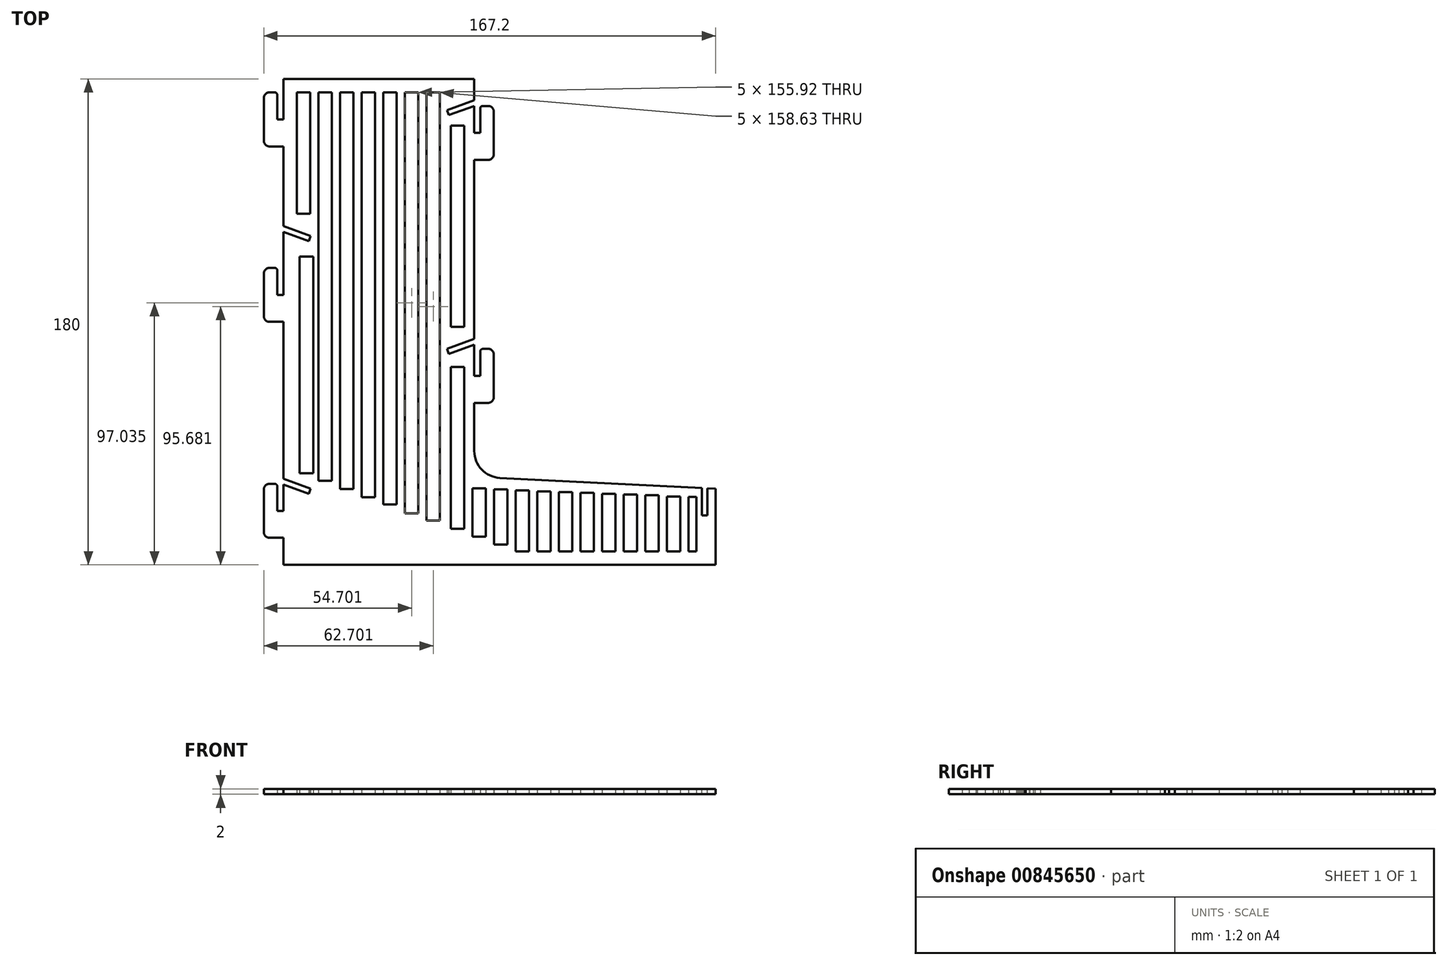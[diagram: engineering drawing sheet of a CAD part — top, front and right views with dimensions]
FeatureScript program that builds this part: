
annotation { "Feature Type Name" : "Feature", "Feature Type Description" : "" }
export const myFeature = defineFeature(function(context is Context, id is Id, definition is map)
    precondition{}
    {
        {
            var Q0;
            Q0=qCreatedBy(makeId("Top.planeOp"),FACE);
            var sketch = newSketch(context, id + "F0", { "sketchPlane" : qUnion([Q0])});
            skLineSegment(sketch, "E0", {"start": v(-80.97, 314.3) * mm, "end": v(-80.97, -331.9) * mm, "construction": true});
            skLineSegment(sketch, "E1", {"start": v(79.03, 327.55) * mm, "end": v(79.03, -337.2) * mm, "construction": true});
            skLineSegment(sketch, "E2", {"start": v(-106.48, 88.93) * mm, "end": v(117.78, 88.93) * mm, "construction": true});
            skLineSegment(sketch, "E3", {"start": v(-139.87, -91.07) * mm, "end": v(208.72, -91.07) * mm, "construction": true});
            skLineSegment(sketch, "E4", {"start": v(-10.29, 120.3) * mm, "end": v(-10.29, -131.57) * mm, "construction": true});
            skLineSegment(sketch, "E5", {"start": v(-224.74, -47.65) * mm, "end": v(82.4, -63.07) * mm, "construction": true});
            skLineSegment(sketch, "E6", {"start": v(-80.97, 88.93) * mm, "end": v(-10.29, 88.93) * mm});
            skLineSegment(sketch, "E7", {"start": v(-10.29, 88.93) * mm, "end": v(-10.29, -58.42) * mm});
            skLineSegment(sketch, "E8", {"start": v(-10.29, -58.42) * mm, "end": v(79.03, -62.9) * mm});
            skLineSegment(sketch, "E9", {"start": v(79.03, -62.9) * mm, "end": v(79.03, -91.07) * mm});
            skLineSegment(sketch, "E10", {"start": v(79.03, -91.07) * mm, "end": v(-80.97, -91.07) * mm});
            skLineSegment(sketch, "E11", {"start": v(-80.97, 88.93) * mm, "end": v(-80.97, -91.07) * mm});
            skSolve(sketch);
        }
        {
            var Q0;
            Q0=qCreatedBy(makeId("Top.planeOp"),FACE);
            var sketch = newSketch(context, id + "F1", { "sketchPlane" : qUnion([Q0])});
            skLineSegment(sketch, "E12.0", {"start": v(-80.97, 88.93) * mm, "end": v(-10.29, 88.93) * mm});
            skLineSegment(sketch, "E12.1", {"start": v(-80.97, 88.93) * mm, "end": v(-80.97, -91.07) * mm});
            skLineSegment(sketch, "E12.2", {"start": v(-10.29, 88.93) * mm, "end": v(-10.29, -48.9) * mm});
            skLineSegment(sketch, "E12.3", {"start": v(-0.79, -58.9) * mm, "end": v(79.03, -62.9) * mm});
            skLineSegment(sketch, "E12.4", {"start": v(79.03, -62.9) * mm, "end": v(79.03, -91.07) * mm});
            skLineSegment(sketch, "E12.5", {"start": v(79.03, -91.07) * mm, "end": v(-80.97, -91.07) * mm});
            skPoint(sketch, "E13.visualSharp", {"position": v(-10.29, -58.42) * mm});
            skArc(sketch, "E13.filletArc", {"start": v(-10.29, -48.9) * mm, "mid": v(-7.53, -55.8) * mm, "end": v(-0.79, -58.9) * mm});
            skSolve(sketch);
        }
        {
            var Q0;
            Q0 = qSketchRegion(id + "F1", true);
            extrude(context, id + "F2", {"entities" : qUnion([Q0]), "depth" : 2 * mm, "offsetDistance" : 25 * mm});
        }
        {
            var Q0;
            Q0=qCreatedBy(makeId("Top.planeOp"),FACE);
            var sketch = newSketch(context, id + "F3", { "sketchPlane" : qUnion([Q0])});
            skLineSegment(sketch, "E14.bottom", {"start": v(-20.37, -11.03) * mm, "end": v(-10.97, -7.61) * mm});
            skLineSegment(sketch, "E14.top", {"start": v(-19.68, -12.91) * mm, "end": v(-10.29, -9.5) * mm});
            skLineSegment(sketch, "E14.left", {"start": v(-20.37, -11.03) * mm, "end": v(-19.68, -12.91) * mm});
            skLineSegment(sketch, "E14.right", {"start": v(-10.97, -7.61) * mm, "end": v(-10.29, -9.5) * mm});
            skLineSegment(sketch, "E15.bottom", {"start": v(-10.97, -7.61) * mm, "end": v(-5.1, -5.47) * mm});
            skLineSegment(sketch, "E15.top", {"start": v(-10.29, -9.5) * mm, "end": v(-4.4, -7.35) * mm});
            skLineSegment(sketch, "E15.right", {"start": v(-5.1, -5.47) * mm, "end": v(-4.4, -7.35) * mm});
            skLineSegment(sketch, "E16.0", {"start": v(-10.29, -9.5) * mm, "end": v(-4.4, -7.35) * mm, "construction": true});
            skLineSegment(sketch, "E17.bottom", {"start": v(-20.37, 77.39) * mm, "end": v(-10.97, 80.8) * mm});
            skLineSegment(sketch, "E17.top", {"start": v(-19.68, 75.5) * mm, "end": v(-10.29, 78.93) * mm});
            skLineSegment(sketch, "E17.left", {"start": v(-20.37, 77.39) * mm, "end": v(-19.68, 75.5) * mm});
            skLineSegment(sketch, "E17.right", {"start": v(-10.97, 80.8) * mm, "end": v(-10.29, 78.93) * mm});
            skLineSegment(sketch, "E18.bottom", {"start": v(-10.97, 80.8) * mm, "end": v(-4, 83.34) * mm});
            skLineSegment(sketch, "E18.top", {"start": v(-10.29, 78.93) * mm, "end": v(-3.31, 81.46) * mm});
            skLineSegment(sketch, "E18.right", {"start": v(-4, 83.34) * mm, "end": v(-3.31, 81.46) * mm});
            skLineSegment(sketch, "E19.0", {"start": v(-10.29, 78.93) * mm, "end": v(-3.31, 81.46) * mm, "construction": true});
            skLineSegment(sketch, "E20.bottom", {"start": v(-71.57, 28.81) * mm, "end": v(-80.97, 32.23) * mm});
            skLineSegment(sketch, "E20.top", {"start": v(-70.89, 30.69) * mm, "end": v(-80.29, 34.1) * mm});
            skLineSegment(sketch, "E20.left", {"start": v(-71.57, 28.81) * mm, "end": v(-70.89, 30.69) * mm});
            skLineSegment(sketch, "E20.right", {"start": v(-80.97, 32.23) * mm, "end": v(-80.29, 34.1) * mm});
            skLineSegment(sketch, "E21.bottom", {"start": v(-80.97, 32.23) * mm, "end": v(-87.94, 34.77) * mm});
            skLineSegment(sketch, "E21.top", {"start": v(-80.29, 34.1) * mm, "end": v(-87.26, 36.65) * mm});
            skLineSegment(sketch, "E21.right", {"start": v(-87.94, 34.77) * mm, "end": v(-87.26, 36.65) * mm});
            skLineSegment(sketch, "E22.0", {"start": v(-87.26, 36.65) * mm, "end": v(-80.29, 34.1) * mm, "construction": true});
            skLineSegment(sketch, "E23.bottom", {"start": v(-71.57, -64.78) * mm, "end": v(-80.97, -61.36) * mm});
            skLineSegment(sketch, "E23.top", {"start": v(-70.89, -62.9) * mm, "end": v(-80.29, -59.48) * mm});
            skLineSegment(sketch, "E23.left", {"start": v(-71.57, -64.78) * mm, "end": v(-70.89, -62.9) * mm});
            skLineSegment(sketch, "E23.right", {"start": v(-80.97, -61.36) * mm, "end": v(-80.29, -59.48) * mm});
            skLineSegment(sketch, "E24.bottom", {"start": v(-80.97, -61.36) * mm, "end": v(-87.94, -58.82) * mm});
            skLineSegment(sketch, "E24.top", {"start": v(-80.29, -59.48) * mm, "end": v(-87.26, -56.94) * mm});
            skLineSegment(sketch, "E24.right", {"start": v(-87.94, -58.82) * mm, "end": v(-87.26, -56.94) * mm});
            skLineSegment(sketch, "E25.0", {"start": v(-87.26, -56.94) * mm, "end": v(-80.29, -59.48) * mm, "construction": true});
            skLineSegment(sketch, "E26.left", {"start": v(-70.89, -62.9) * mm, "end": v(-71.64, -64.97) * mm});
            skLineSegment(sketch, "E27.bottom", {"start": v(74.03, -72.75) * mm, "end": v(74.03, -62.75) * mm});
            skLineSegment(sketch, "E27.top", {"start": v(76.03, -72.75) * mm, "end": v(76.03, -62.75) * mm});
            skLineSegment(sketch, "E27.left", {"start": v(74.03, -72.75) * mm, "end": v(76.03, -72.75) * mm});
            skLineSegment(sketch, "E27.right", {"start": v(74.03, -62.75) * mm, "end": v(76.03, -62.75) * mm});
            skLineSegment(sketch, "E28.bottom", {"start": v(74.03, -62.75) * mm, "end": v(74.03, -55.33) * mm});
            skLineSegment(sketch, "E28.top", {"start": v(76.03, -62.75) * mm, "end": v(76.03, -55.33) * mm});
            skLineSegment(sketch, "E28.right", {"start": v(74.03, -55.33) * mm, "end": v(76.03, -55.33) * mm});
            skLineSegment(sketch, "E29.0", {"start": v(76.03, -55.33) * mm, "end": v(76.03, -62.75) * mm, "construction": true});
            skSolve(sketch);
        }
        {
            var Q0;
            {var subQ0=makeQuery(id+"F3.imprint","IMPRINT",EDGE,{"derivedFrom":sQuery(id+"F3.wireOp",EDGE,"E27.right")});var subQ1=makeQuery(id+"F3.imprint","IMPRINT",EDGE,{"derivedFrom":sQuery(id+"F3.wireOp",EDGE,"E23.right")});var subQ2=makeQuery(id+"F3.imprint","IMPRINT",EDGE,{"derivedFrom":sQuery(id+"F3.wireOp",EDGE,"E20.right")});var subQ3=makeQuery(id+"F3.imprint","IMPRINT",EDGE,{"derivedFrom":sQuery(id+"F3.wireOp",EDGE,"E17.right")});var subQ4=makeQuery(id+"F3.imprint","IMPRINT",EDGE,{"derivedFrom":sQuery(id+"F3.wireOp",EDGE,"E14.right")});Q0=qUnion([makeQuery(id+"F3.imprint","IMPRINT",FACE,{"disambiguationData":[TD([[makeQuery(id+"F3.imprint","IMPRINT",EDGE,{"derivedFrom":sQuery(id+"F3.wireOp",EDGE,"E14.bottom")}),-1.0]])]}),makeQuery(id+"F3.imprint","IMPRINT",FACE,{"disambiguationData":[TD([[subQ4,1.0]])]}),makeQuery(id+"F3.imprint","IMPRINT",FACE,{"disambiguationData":[TD([[makeQuery(id+"F3.imprint","IMPRINT",EDGE,{"derivedFrom":sQuery(id+"F3.wireOp",EDGE,"E17.bottom")}),-1.0]])]}),makeQuery(id+"F3.imprint","IMPRINT",FACE,{"disambiguationData":[TD([[subQ3,1.0]])]}),makeQuery(id+"F3.imprint","IMPRINT",FACE,{"disambiguationData":[TD([[makeQuery(id+"F3.imprint","IMPRINT",EDGE,{"derivedFrom":sQuery(id+"F3.wireOp",EDGE,"E20.bottom")}),-1.0]])]}),makeQuery(id+"F3.imprint","IMPRINT",FACE,{"disambiguationData":[TD([[subQ2,1.0]])]}),makeQuery(id+"F3.imprint","IMPRINT",FACE,{"disambiguationData":[TD([[makeQuery(id+"F3.imprint","IMPRINT",EDGE,{"derivedFrom":sQuery(id+"F3.wireOp",EDGE,"E23.bottom")}),-1.0]])]}),makeQuery(id+"F3.imprint","IMPRINT",FACE,{"disambiguationData":[TD([[subQ1,1.0]])]}),makeQuery(id+"F3.imprint","IMPRINT",FACE,{"disambiguationData":[TD([[makeQuery(id+"F3.imprint","IMPRINT",EDGE,{"derivedFrom":sQuery(id+"F3.wireOp",EDGE,"E27.bottom")}),-1.0]])]}),makeQuery(id+"F3.imprint","IMPRINT",FACE,{"disambiguationData":[TD([[subQ0,1.0]])]})]);}
            extrude(context, id + "F4", {"entities" : qUnion([Q0]), "operationType" : NewBodyOperationType.REMOVE, "depth" : 25 * mm, "offsetDistance" : 25 * mm});
        }
        {
            var Q0;
            Q0=qCreatedBy(makeId("Top.planeOp"),FACE);
            var sketch = newSketch(context, id + "F5", { "sketchPlane" : qUnion([Q0])});
            skLineSegment(sketch, "E30", {"start": v(-86.17, -61.07) * mm, "end": v(-84.2, -61.07) * mm});
            skLineSegment(sketch, "E31", {"start": v(-83.17, -62.1) * mm, "end": v(-83.17, -71.07) * mm});
            skPoint(sketch, "E31.endSnap0", {"position": v(-84.58, -71.07) * mm});
            skLineSegment(sketch, "E32", {"start": v(-83.17, -71.07) * mm, "end": v(-80.97, -71.07) * mm});
            skLineSegment(sketch, "E33", {"start": v(-80.97, -71.07) * mm, "end": v(-80.97, -81.07) * mm});
            skLineSegment(sketch, "E34", {"start": v(-80.97, -81.07) * mm, "end": v(-83.17, -81.07) * mm});
            skLineSegment(sketch, "E35", {"start": v(-83.17, -81.07) * mm, "end": v(-86.17, -81.07) * mm});
            skLineSegment(sketch, "E36", {"start": v(-88.17, -79.07) * mm, "end": v(-88.17, -63.07) * mm});
            skPoint(sketch, "E37.visualSharp", {"position": v(-83.17, -61.07) * mm});
            skArc(sketch, "E37.filletArc", {"start": v(-83.17, -62.1) * mm, "mid": v(-83.47, -61.37) * mm, "end": v(-84.2, -61.07) * mm});
            skPoint(sketch, "E38.visualSharp", {"position": v(-88.17, -61.07) * mm});
            skArc(sketch, "E38.filletArc", {"start": v(-86.17, -61.07) * mm, "mid": v(-87.58, -61.66) * mm, "end": v(-88.17, -63.07) * mm});
            skPoint(sketch, "E39.visualSharp", {"position": v(-88.17, -81.07) * mm});
            skArc(sketch, "E39.filletArc", {"start": v(-88.17, -79.07) * mm, "mid": v(-87.58, -80.49) * mm, "end": v(-86.17, -81.07) * mm});
            skLineSegment(sketch, "E40", {"start": v(-86.17, 18.93) * mm, "end": v(-84.2, 18.93) * mm});
            skLineSegment(sketch, "E41", {"start": v(-83.17, 17.9) * mm, "end": v(-83.17, 8.93) * mm});
            skPoint(sketch, "E41.endSnap0", {"position": v(-84.58, 8.93) * mm});
            skLineSegment(sketch, "E42", {"start": v(-83.17, 8.93) * mm, "end": v(-80.97, 8.93) * mm});
            skLineSegment(sketch, "E43", {"start": v(-80.97, 8.93) * mm, "end": v(-80.97, -1.07) * mm});
            skLineSegment(sketch, "E44", {"start": v(-80.97, -1.07) * mm, "end": v(-83.17, -1.07) * mm});
            skLineSegment(sketch, "E45", {"start": v(-83.17, -1.07) * mm, "end": v(-86.17, -1.07) * mm});
            skLineSegment(sketch, "E46", {"start": v(-88.17, 0.93) * mm, "end": v(-88.17, 16.93) * mm});
            skPoint(sketch, "E47.visualSharp", {"position": v(-83.17, 18.93) * mm});
            skArc(sketch, "E47.filletArc", {"start": v(-83.17, 17.9) * mm, "mid": v(-83.47, 18.63) * mm, "end": v(-84.2, 18.93) * mm});
            skPoint(sketch, "E48.visualSharp", {"position": v(-88.17, 18.93) * mm});
            skArc(sketch, "E48.filletArc", {"start": v(-86.17, 18.93) * mm, "mid": v(-87.58, 18.34) * mm, "end": v(-88.17, 16.93) * mm});
            skPoint(sketch, "E49.visualSharp", {"position": v(-88.17, -1.07) * mm});
            skArc(sketch, "E49.filletArc", {"start": v(-88.17, 0.93) * mm, "mid": v(-87.58, -0.49) * mm, "end": v(-86.17, -1.07) * mm});
            skLineSegment(sketch, "E50", {"start": v(-86.17, 83.93) * mm, "end": v(-84.2, 83.93) * mm});
            skLineSegment(sketch, "E51", {"start": v(-83.17, 82.9) * mm, "end": v(-83.17, 73.93) * mm});
            skPoint(sketch, "E51.endSnap0", {"position": v(-84.58, 73.93) * mm});
            skLineSegment(sketch, "E52", {"start": v(-83.17, 73.93) * mm, "end": v(-80.97, 73.93) * mm});
            skLineSegment(sketch, "E53", {"start": v(-80.97, 73.93) * mm, "end": v(-80.97, 63.93) * mm});
            skLineSegment(sketch, "E54", {"start": v(-80.97, 63.93) * mm, "end": v(-86.97, 63.93) * mm});
            skLineSegment(sketch, "E55", {"start": v(-86.17, 63.93) * mm, "end": v(-86.97, 63.93) * mm});
            skLineSegment(sketch, "E56", {"start": v(-88.17, 65.93) * mm, "end": v(-88.17, 81.93) * mm});
            skPoint(sketch, "E57.visualSharp", {"position": v(-83.17, 83.93) * mm});
            skArc(sketch, "E57.filletArc", {"start": v(-83.17, 82.9) * mm, "mid": v(-83.47, 83.63) * mm, "end": v(-84.2, 83.93) * mm});
            skPoint(sketch, "E58.visualSharp", {"position": v(-88.17, 83.93) * mm});
            skArc(sketch, "E58.filletArc", {"start": v(-86.17, 83.93) * mm, "mid": v(-87.58, 83.34) * mm, "end": v(-88.17, 81.93) * mm});
            skPoint(sketch, "E59.visualSharp", {"position": v(-88.17, 63.93) * mm});
            skArc(sketch, "E59.filletArc", {"start": v(-88.17, 65.93) * mm, "mid": v(-87.58, 64.51) * mm, "end": v(-86.17, 63.93) * mm});
            skLineSegment(sketch, "E60", {"start": v(-9.8, 58.93) * mm, "end": v(-7.6, 58.93) * mm});
            skLineSegment(sketch, "E61", {"start": v(-7.6, 58.93) * mm, "end": v(-4.6, 58.93) * mm});
            skLineSegment(sketch, "E62.MirrorCS", {"start": v(-10.29, 58.93) * mm, "end": v(-8.09, 58.93) * mm});
            skLineSegment(sketch, "E63.MirrorCS", {"start": v(-8.09, 58.93) * mm, "end": v(-5.09, 58.93) * mm});
            skArc(sketch, "E64.MirrorCS", {"start": v(-8.09, 77.9) * mm, "mid": v(-7.79, 78.63) * mm, "end": v(-7.07, 78.93) * mm});
            skLineSegment(sketch, "E65.MirrorCS", {"start": v(-8.09, 68.93) * mm, "end": v(-10.29, 68.93) * mm});
            skLineSegment(sketch, "E66.MirrorCS", {"start": v(-5.09, 78.93) * mm, "end": v(-7.07, 78.93) * mm});
            skArc(sketch, "E67.MirrorCS", {"start": v(-3.09, 60.93) * mm, "mid": v(-3.67, 59.51) * mm, "end": v(-5.09, 58.93) * mm});
            skArc(sketch, "E68.MirrorCS", {"start": v(-5.09, 78.93) * mm, "mid": v(-3.67, 78.34) * mm, "end": v(-3.09, 76.93) * mm});
            skPoint(sketch, "E69.MirrorP", {"position": v(-6.2, 66.96) * mm});
            skLineSegment(sketch, "E70.MirrorCS", {"start": v(-10.29, 68.93) * mm, "end": v(-10.29, 58.93) * mm});
            skPoint(sketch, "E71.MirrorP", {"position": v(-7.6, 76.96) * mm});
            skLineSegment(sketch, "E72.MirrorCS", {"start": v(-3.09, 60.93) * mm, "end": v(-3.09, 76.93) * mm});
            skLineSegment(sketch, "E73.MirrorCS", {"start": v(-8.09, 77.9) * mm, "end": v(-8.09, 68.93) * mm});
            skLineSegment(sketch, "E74.MirrorCS", {"start": v(-10.29, -31.07) * mm, "end": v(-8.09, -31.07) * mm});
            skLineSegment(sketch, "E75.MirrorCS", {"start": v(-8.09, -31.07) * mm, "end": v(-5.09, -31.07) * mm});
            skArc(sketch, "E76.MirrorCS", {"start": v(-8.09, -12.1) * mm, "mid": v(-7.79, -11.37) * mm, "end": v(-7.07, -11.07) * mm});
            skLineSegment(sketch, "E77.MirrorCS", {"start": v(-8.09, -21.07) * mm, "end": v(-10.29, -21.07) * mm});
            skLineSegment(sketch, "E78.MirrorCS", {"start": v(-5.09, -11.07) * mm, "end": v(-7.07, -11.07) * mm});
            skArc(sketch, "E79.MirrorCS", {"start": v(-3.09, -29.07) * mm, "mid": v(-3.67, -30.49) * mm, "end": v(-5.09, -31.07) * mm});
            skArc(sketch, "E80.MirrorCS", {"start": v(-5.09, -11.07) * mm, "mid": v(-3.67, -11.66) * mm, "end": v(-3.09, -13.07) * mm});
            skLineSegment(sketch, "E81.MirrorCS", {"start": v(-10.29, -21.07) * mm, "end": v(-10.29, -31.07) * mm});
            skLineSegment(sketch, "E82.MirrorCS", {"start": v(-3.09, -29.07) * mm, "end": v(-3.09, -13.07) * mm});
            skLineSegment(sketch, "E83.MirrorCS", {"start": v(-8.09, -12.1) * mm, "end": v(-8.09, -21.07) * mm});
            skLineSegment(sketch, "E84", {"start": v(-84.24, 88.93) * mm, "end": v(12.8, 88.93) * mm, "construction": true});
            skSolve(sketch);
        }
        {
            var Q0;
            Q0 = qSketchRegion(id + "F5", true);
            extrude(context, id + "F6", {"entities" : qUnion([Q0]), "operationType" : NewBodyOperationType.ADD, "depth" : 2 * mm, "offsetDistance" : 25 * mm});
        }
        {
            var Q0;
            Q0=qCreatedBy(makeId("Top.planeOp"),FACE);
            var sketch = newSketch(context, id + "F7", { "sketchPlane" : qUnion([Q0])});
            skLineSegment(sketch, "E85.bottom", {"start": v(-75.97, 83.93) * mm, "end": v(-70.97, 83.93) * mm});
            skLineSegment(sketch, "E85.top", {"start": v(-75.97, 39) * mm, "end": v(-70.97, 39) * mm});
            skLineSegment(sketch, "E85.left", {"start": v(-75.97, 83.93) * mm, "end": v(-75.97, 39) * mm});
            skLineSegment(sketch, "E85.right", {"start": v(-70.97, 83.93) * mm, "end": v(-70.97, 39) * mm});
            skLineSegment(sketch, "E86.bottom", {"start": v(-74.91, 23.13) * mm, "end": v(-69.91, 23.13) * mm});
            skLineSegment(sketch, "E86.top", {"start": v(-74.91, -57.15) * mm, "end": v(-69.91, -57.15) * mm});
            skLineSegment(sketch, "E86.left", {"start": v(-74.91, 23.13) * mm, "end": v(-74.91, -57.15) * mm});
            skLineSegment(sketch, "E86.right", {"start": v(-69.91, 23.13) * mm, "end": v(-69.91, -57.15) * mm});
            skLineSegment(sketch, "E87.bottom", {"start": v(-67.97, 83.93) * mm, "end": v(-62.97, 83.93) * mm});
            skLineSegment(sketch, "E87.top", {"start": v(-67.97, -59.9) * mm, "end": v(-62.97, -59.9) * mm});
            skLineSegment(sketch, "E87.left", {"start": v(-67.97, 83.93) * mm, "end": v(-67.97, -59.9) * mm});
            skLineSegment(sketch, "E87.right", {"start": v(-62.97, 83.93) * mm, "end": v(-62.97, -59.9) * mm});
            skLineSegment(sketch, "E88.bottom", {"start": v(-59.97, 83.93) * mm, "end": v(-54.97, 83.93) * mm});
            skLineSegment(sketch, "E88.top", {"start": v(-59.97, -62.99) * mm, "end": v(-54.97, -62.99) * mm});
            skLineSegment(sketch, "E88.left", {"start": v(-59.97, 83.93) * mm, "end": v(-59.97, -62.99) * mm});
            skLineSegment(sketch, "E88.right", {"start": v(-54.97, 83.93) * mm, "end": v(-54.97, -62.99) * mm});
            skLineSegment(sketch, "E89.bottom", {"start": v(-51.97, 83.93) * mm, "end": v(-46.97, 83.93) * mm});
            skLineSegment(sketch, "E89.top", {"start": v(-51.97, -66.08) * mm, "end": v(-46.97, -66.08) * mm});
            skLineSegment(sketch, "E89.left", {"start": v(-51.97, 83.93) * mm, "end": v(-51.97, -66.08) * mm});
            skLineSegment(sketch, "E89.right", {"start": v(-46.97, 83.93) * mm, "end": v(-46.97, -66.08) * mm});
            skLineSegment(sketch, "E90.bottom", {"start": v(-35.97, 83.93) * mm, "end": v(-30.97, 83.93) * mm});
            skLineSegment(sketch, "E90.top", {"start": v(-35.97, -72) * mm, "end": v(-30.97, -72) * mm});
            skLineSegment(sketch, "E90.left", {"start": v(-35.97, 83.93) * mm, "end": v(-35.97, -72) * mm});
            skLineSegment(sketch, "E90.right", {"start": v(-30.97, 83.93) * mm, "end": v(-30.97, -72) * mm});
            skLineSegment(sketch, "E91.bottom", {"start": v(-43.97, 83.93) * mm, "end": v(-38.97, 83.93) * mm});
            skLineSegment(sketch, "E91.top", {"start": v(-43.97, -68.68) * mm, "end": v(-38.97, -68.68) * mm});
            skLineSegment(sketch, "E91.left", {"start": v(-43.97, 83.93) * mm, "end": v(-43.97, -68.68) * mm});
            skLineSegment(sketch, "E91.right", {"start": v(-38.97, 83.93) * mm, "end": v(-38.97, -68.68) * mm});
            skLineSegment(sketch, "E92.bottom", {"start": v(-27.97, 83.93) * mm, "end": v(-22.97, 83.93) * mm});
            skLineSegment(sketch, "E92.top", {"start": v(-27.97, -74.7) * mm, "end": v(-22.97, -74.7) * mm});
            skLineSegment(sketch, "E92.left", {"start": v(-27.97, 83.93) * mm, "end": v(-27.97, -74.7) * mm});
            skLineSegment(sketch, "E92.right", {"start": v(-22.97, 83.93) * mm, "end": v(-22.97, -74.7) * mm});
            skLineSegment(sketch, "E93", {"start": v(-119.56, -41.14) * mm, "end": v(40.75, -99.49) * mm, "construction": true});
            skLineSegment(sketch, "E94.bottom", {"start": v(-18.97, 71.67) * mm, "end": v(-13.97, 71.67) * mm});
            skLineSegment(sketch, "E94.top", {"start": v(-18.97, -2.9) * mm, "end": v(-13.97, -2.9) * mm});
            skLineSegment(sketch, "E94.left", {"start": v(-18.97, 71.67) * mm, "end": v(-18.97, -2.9) * mm});
            skLineSegment(sketch, "E94.right", {"start": v(-13.97, 71.67) * mm, "end": v(-13.97, -2.9) * mm});
            skLineSegment(sketch, "E95.bottom", {"start": v(-18.97, -17.75) * mm, "end": v(-13.97, -17.75) * mm});
            skLineSegment(sketch, "E95.top", {"start": v(-18.97, -77.69) * mm, "end": v(-13.97, -77.69) * mm});
            skLineSegment(sketch, "E95.left", {"start": v(-18.97, -17.75) * mm, "end": v(-18.97, -77.69) * mm});
            skLineSegment(sketch, "E95.right", {"start": v(-13.97, -17.75) * mm, "end": v(-13.97, -77.69) * mm});
            skLineSegment(sketch, "E96", {"start": v(-65.77, -60.36) * mm, "end": v(104.69, -67.23) * mm, "construction": true});
            skLineSegment(sketch, "E97.bottom", {"start": v(-10.97, -62.8) * mm, "end": v(-5.97, -62.8) * mm});
            skLineSegment(sketch, "E97.top", {"start": v(-10.97, -80.6) * mm, "end": v(-5.97, -80.6) * mm});
            skLineSegment(sketch, "E97.left", {"start": v(-10.97, -62.8) * mm, "end": v(-10.97, -80.6) * mm});
            skLineSegment(sketch, "E97.right", {"start": v(-5.97, -62.8) * mm, "end": v(-5.97, -80.6) * mm});
            skLineSegment(sketch, "E98.bottom", {"start": v(-2.97, -63.14) * mm, "end": v(2.03, -63.14) * mm});
            skLineSegment(sketch, "E98.top", {"start": v(-2.97, -83.62) * mm, "end": v(2.03, -83.62) * mm});
            skLineSegment(sketch, "E98.left", {"start": v(-2.97, -63.14) * mm, "end": v(-2.97, -83.62) * mm});
            skLineSegment(sketch, "E98.right", {"start": v(2.03, -63.14) * mm, "end": v(2.03, -83.62) * mm});
            skLineSegment(sketch, "E99.bottom", {"start": v(5.03, -63.46) * mm, "end": v(10.03, -63.46) * mm});
            skLineSegment(sketch, "E99.top", {"start": v(5.03, -86.07) * mm, "end": v(10.03, -86.07) * mm});
            skLineSegment(sketch, "E99.left", {"start": v(5.03, -63.46) * mm, "end": v(5.03, -86.07) * mm});
            skLineSegment(sketch, "E99.right", {"start": v(10.03, -63.46) * mm, "end": v(10.03, -86.07) * mm});
            skLineSegment(sketch, "E100.bottom", {"start": v(13.03, -63.87) * mm, "end": v(18.03, -63.87) * mm});
            skLineSegment(sketch, "E100.top", {"start": v(13.03, -86.07) * mm, "end": v(18.03, -86.07) * mm});
            skLineSegment(sketch, "E100.left", {"start": v(13.03, -63.87) * mm, "end": v(13.03, -86.07) * mm});
            skLineSegment(sketch, "E100.right", {"start": v(18.03, -63.87) * mm, "end": v(18.03, -86.07) * mm});
            skLineSegment(sketch, "E101.bottom", {"start": v(21.03, -64.15) * mm, "end": v(26.03, -64.15) * mm});
            skLineSegment(sketch, "E101.top", {"start": v(21.03, -86.07) * mm, "end": v(26.03, -86.07) * mm});
            skLineSegment(sketch, "E101.left", {"start": v(21.03, -64.15) * mm, "end": v(21.03, -86.07) * mm});
            skLineSegment(sketch, "E101.right", {"start": v(26.03, -64.15) * mm, "end": v(26.03, -86.07) * mm});
            skLineSegment(sketch, "E102.bottom", {"start": v(29.03, -64.43) * mm, "end": v(34.03, -64.43) * mm});
            skLineSegment(sketch, "E102.top", {"start": v(29.03, -86.07) * mm, "end": v(34.03, -86.07) * mm});
            skLineSegment(sketch, "E102.left", {"start": v(29.03, -64.43) * mm, "end": v(29.03, -86.07) * mm});
            skLineSegment(sketch, "E102.right", {"start": v(34.03, -64.43) * mm, "end": v(34.03, -86.07) * mm});
            skLineSegment(sketch, "E103.bottom", {"start": v(37.03, -64.77) * mm, "end": v(42.03, -64.77) * mm});
            skLineSegment(sketch, "E103.top", {"start": v(37.03, -86.07) * mm, "end": v(42.03, -86.07) * mm});
            skLineSegment(sketch, "E103.left", {"start": v(37.03, -64.77) * mm, "end": v(37.03, -86.07) * mm});
            skLineSegment(sketch, "E103.right", {"start": v(42.03, -64.77) * mm, "end": v(42.03, -86.07) * mm});
            skLineSegment(sketch, "E104.bottom", {"start": v(45.03, -65.04) * mm, "end": v(50.03, -65.04) * mm});
            skLineSegment(sketch, "E104.top", {"start": v(45.03, -86.07) * mm, "end": v(50.03, -86.07) * mm});
            skLineSegment(sketch, "E104.left", {"start": v(45.03, -65.04) * mm, "end": v(45.03, -86.07) * mm});
            skLineSegment(sketch, "E104.right", {"start": v(50.03, -65.04) * mm, "end": v(50.03, -86.07) * mm});
            skLineSegment(sketch, "E105.bottom", {"start": v(53.03, -65.3) * mm, "end": v(58.03, -65.3) * mm});
            skLineSegment(sketch, "E105.top", {"start": v(53.03, -86.07) * mm, "end": v(58.03, -86.07) * mm});
            skLineSegment(sketch, "E105.left", {"start": v(53.03, -65.3) * mm, "end": v(53.03, -86.07) * mm});
            skLineSegment(sketch, "E105.right", {"start": v(58.03, -65.3) * mm, "end": v(58.03, -86.07) * mm});
            skLineSegment(sketch, "E106.bottom", {"start": v(61.03, -65.73) * mm, "end": v(66.03, -65.73) * mm});
            skLineSegment(sketch, "E106.top", {"start": v(61.03, -86.07) * mm, "end": v(66.03, -86.07) * mm});
            skLineSegment(sketch, "E106.left", {"start": v(61.03, -65.73) * mm, "end": v(61.03, -86.07) * mm});
            skLineSegment(sketch, "E106.right", {"start": v(66.03, -65.73) * mm, "end": v(66.03, -86.07) * mm});
            skLineSegment(sketch, "E107.bottom", {"start": v(69.03, -65.93) * mm, "end": v(72.03, -65.93) * mm});
            skLineSegment(sketch, "E107.top", {"start": v(69.03, -86.07) * mm, "end": v(72.03, -86.07) * mm});
            skLineSegment(sketch, "E107.left", {"start": v(69.03, -65.93) * mm, "end": v(69.03, -86.07) * mm});
            skLineSegment(sketch, "E107.right", {"start": v(72.03, -65.93) * mm, "end": v(72.03, -86.07) * mm});
            skSolve(sketch);
        }
        {
            var Q0;
            Q0 = qSketchRegion(id + "F7", true);
            extrude(context, id + "F8", {"entities" : qUnion([Q0]), "operationType" : NewBodyOperationType.REMOVE, "depth" : 5 * mm, "offsetDistance" : 25 * mm});
        }
    });
